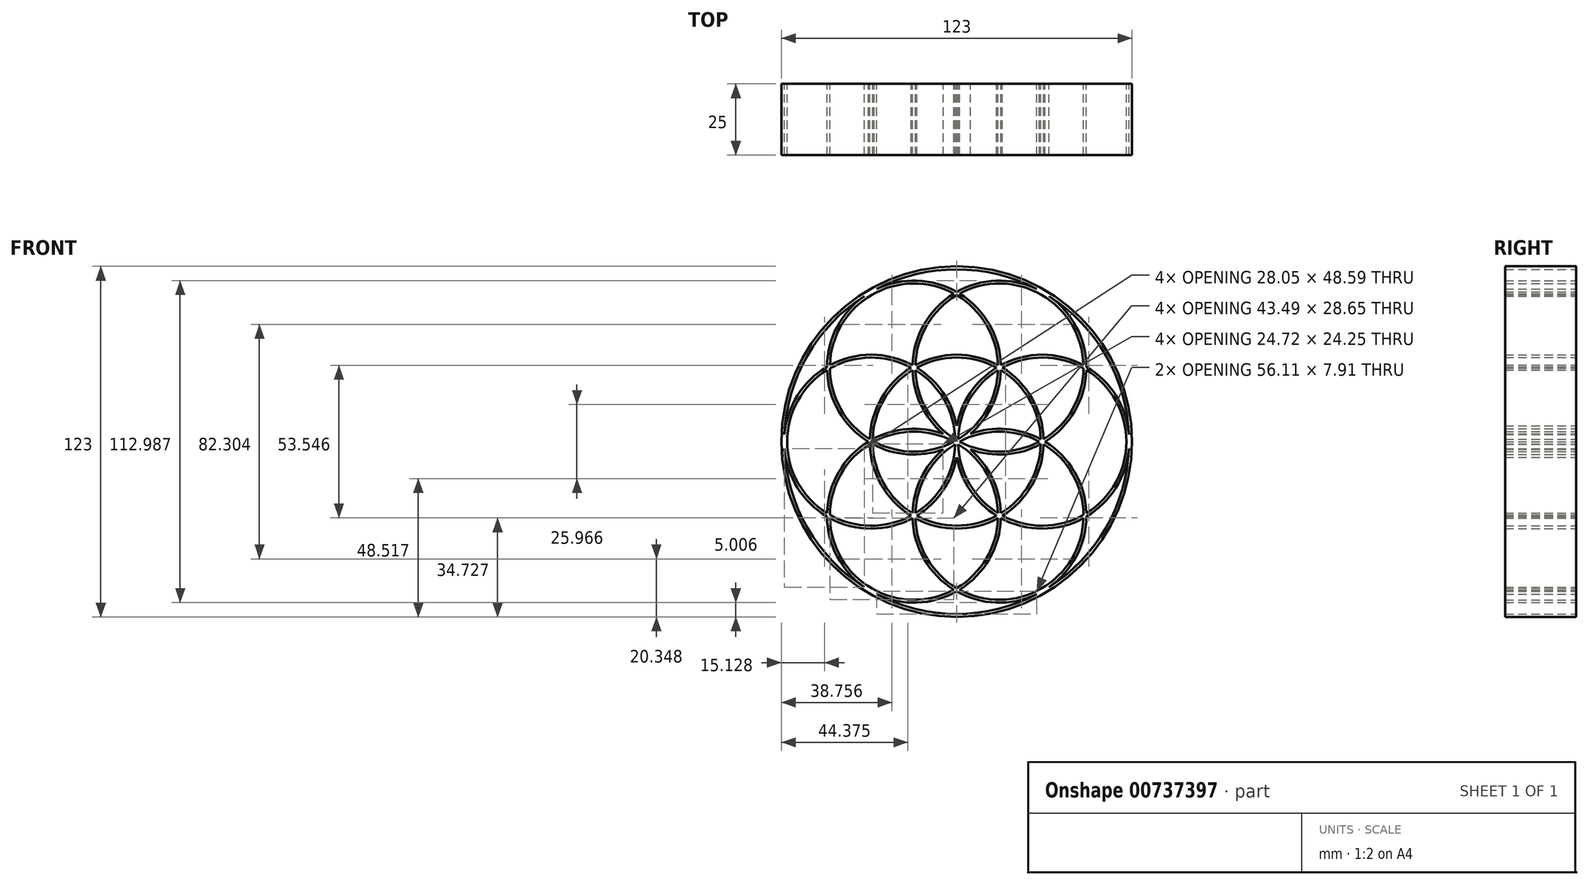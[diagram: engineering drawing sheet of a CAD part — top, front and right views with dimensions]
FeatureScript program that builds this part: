
annotation { "Feature Type Name" : "Feature", "Feature Type Description" : "" }
export const myFeature = defineFeature(function(context is Context, id is Id, definition is map)
    precondition{}
    {
        {
            var Q0;
            Q0=qCreatedBy(makeId("Front.planeOp"),FACE);
            var sketch = newSketch(context, id + "F0", { "sketchPlane" : qUnion([Q0])});
            skArc(sketch, "E0", {"start": v(14.49, 26.84) * mm, "mid": v(0, 30.5) * mm, "end": v(-14.49, 26.84) * mm});
            skArc(sketch, "E1", {"start": v(14, 25.97) * mm, "mid": v(0, 29.5) * mm, "end": v(-14, 25.97) * mm});
            skCircle(sketch, "E2", {"center": v(0, 0) * mm, "radius": 30 * mm, "construction": true});
            skLineSegment(sketch, "E3", {"start": v(0, 0) * mm, "end": v(0, 50.88) * mm, "construction": true});
            skLineSegment(sketch, "E4", {"start": v(0, 0) * mm, "end": v(-40.85, 0) * mm, "construction": true});
            skLineSegment(sketch, "E5", {"start": v(0, 0) * mm, "end": v(-19.65, 34.03) * mm, "construction": true});
            skCircle(sketch, "E6", {"center": v(-15, 25.98) * mm, "radius": 30 * mm, "construction": true});
            skArc(sketch, "E7.1.0", {"start": v(0, 5.5) * mm, "mid": v(-4.83, 17.22) * mm, "end": v(-14, 25.97) * mm});
            skCircle(sketch, "E7.1.1", {"center": v(-30, 0) * mm, "radius": 30 * mm, "construction": true});
            skCircle(sketch, "E7.2.1", {"center": v(-15, -25.98) * mm, "radius": 30 * mm, "construction": true});
            skArc(sketch, "E7.3.0", {"start": v(-4.76, -2.75) * mm, "mid": v(-12.5, -12.79) * mm, "end": v(-15.49, -25.1) * mm});
            skCircle(sketch, "E7.3.1", {"center": v(15, -25.98) * mm, "radius": 30 * mm, "construction": true});
            skCircle(sketch, "E7.4.1", {"center": v(30, 0) * mm, "radius": 30 * mm, "construction": true});
            skArc(sketch, "E7.4.2", {"start": v(0.51, -0.89) * mm, "mid": v(4.45, -14.75) * mm, "end": v(14.49, -25.1) * mm});
            skArc(sketch, "E7.5.0", {"start": v(4.76, -2.75) * mm, "mid": v(17.33, -4.43) * mm, "end": v(29.49, -0.86) * mm});
            skCircle(sketch, "E7.5.1", {"center": v(15, 25.98) * mm, "radius": 30 * mm, "construction": true});
            skArc(sketch, "E7.5.2", {"start": v(1.03, 0) * mm, "mid": v(15, -3.52) * mm, "end": v(28.97, 0) * mm});
            skArc(sketch, "E8.trimOffspring", {"start": v(0, -5.5) * mm, "mid": v(4.83, -17.22) * mm, "end": v(14, -25.97) * mm});
            skArc(sketch, "E9.trimOffspring", {"start": v(-4.76, 2.75) * mm, "mid": v(-17.33, 4.43) * mm, "end": v(-29.49, 0.86) * mm});
            skArc(sketch, "E10.trimOffspring", {"start": v(4.76, 2.75) * mm, "mid": v(12.5, 12.79) * mm, "end": v(15.49, 25.1) * mm});
            skArc(sketch, "E11.trimOffspring", {"start": v(0.51, 0.89) * mm, "mid": v(10.55, 11.23) * mm, "end": v(14.49, 25.1) * mm});
            skArc(sketch, "E12.trimOffspring", {"start": v(-0.5, -0.9) * mm, "mid": v(-10.53, -11.24) * mm, "end": v(-14.47, -25.1) * mm});
            skArc(sketch, "E13.trimOffspring", {"start": v(-1.03, 0) * mm, "mid": v(-15, 3.52) * mm, "end": v(-28.97, 0) * mm});
            skArc(sketch, "E14.trimOffspring", {"start": v(-0.5, 0.88) * mm, "mid": v(-4.44, 14.75) * mm, "end": v(-14.49, 25.1) * mm});
            skArc(sketch, "E15.trimOffspring", {"start": v(14.49, 26.84) * mm, "mid": v(10.4, 40.98) * mm, "end": v(0, 51.38) * mm});
            skArc(sketch, "E16.trimOffspring", {"start": v(15.49, 26.83) * mm, "mid": v(11.42, 41.22) * mm, "end": v(1, 51.95) * mm});
            skArc(sketch, "E17.trimOffspring", {"start": v(14, 25.97) * mm, "mid": v(4.83, 17.22) * mm, "end": v(0, 5.5) * mm});
            skArc(sketch, "E18.trimOffspring", {"start": v(14.49, 25.1) * mm, "mid": v(4.45, 14.75) * mm, "end": v(0.51, 0.89) * mm});
            skArc(sketch, "E19.trimOffspring", {"start": v(30.98, 0) * mm, "mid": v(41.4, 10.72) * mm, "end": v(45.49, 25.1) * mm});
            skArc(sketch, "E20.trimOffspring", {"start": v(28.97, 0) * mm, "mid": v(15, 3.52) * mm, "end": v(1.03, 0) * mm});
            skArc(sketch, "E21.trimOffspring", {"start": v(30.49, 0.87) * mm, "mid": v(40.69, 11.48) * mm, "end": v(44.5, 25.7) * mm});
            skArc(sketch, "E22.trimOffspring", {"start": v(29.49, 0.86) * mm, "mid": v(17.33, 4.43) * mm, "end": v(4.76, 2.75) * mm});
            skArc(sketch, "E23.trimOffspring", {"start": v(30.49, 0.87) * mm, "mid": v(26.41, 15.25) * mm, "end": v(16, 25.97) * mm});
            skArc(sketch, "E24.trimOffspring", {"start": v(29.49, 0.86) * mm, "mid": v(25.55, 14.75) * mm, "end": v(15.49, 25.1) * mm});
            skArc(sketch, "E25.trimOffspring", {"start": v(14.49, -25.1) * mm, "mid": v(10.55, -11.23) * mm, "end": v(0.51, -0.89) * mm});
            skArc(sketch, "E26.trimOffspring", {"start": v(15.49, -25.1) * mm, "mid": v(25.55, -14.75) * mm, "end": v(29.49, -0.86) * mm});
            skArc(sketch, "E27.trimOffspring", {"start": v(15.49, -25.1) * mm, "mid": v(12.5, -12.79) * mm, "end": v(4.76, -2.75) * mm});
            skArc(sketch, "E28.trimOffspring", {"start": v(16, -25.97) * mm, "mid": v(30.28, -29.5) * mm, "end": v(44.5, -25.7) * mm});
            skArc(sketch, "E29.trimOffspring", {"start": v(16, -25.97) * mm, "mid": v(26.41, -15.25) * mm, "end": v(30.49, -0.87) * mm});
            skArc(sketch, "E30.trimOffspring", {"start": v(15.49, -26.83) * mm, "mid": v(29.99, -30.5) * mm, "end": v(44.49, -26.84) * mm});
            skArc(sketch, "E31.trimOffspring", {"start": v(-14.47, -25.1) * mm, "mid": v(-4.44, -14.76) * mm, "end": v(-0.5, -0.9) * mm});
            skArc(sketch, "E32.trimOffspring", {"start": v(-14, -25.97) * mm, "mid": v(0, -29.5) * mm, "end": v(14, -25.97) * mm});
            skArc(sketch, "E33.trimOffspring", {"start": v(-15.49, -26.83) * mm, "mid": v(-11.42, -41.22) * mm, "end": v(-1, -51.95) * mm});
            skArc(sketch, "E34.trimOffspring", {"start": v(-14.49, -26.84) * mm, "mid": v(0, -30.5) * mm, "end": v(14.49, -26.84) * mm});
            skArc(sketch, "E35.trimOffspring", {"start": v(-14.49, -26.84) * mm, "mid": v(-10.4, -40.98) * mm, "end": v(0, -51.38) * mm});
            skArc(sketch, "E36.trimOffspring", {"start": v(-14, -25.97) * mm, "mid": v(-4.83, -17.22) * mm, "end": v(0, -5.5) * mm});
            skArc(sketch, "E37.trimOffspring", {"start": v(-30.98, 0) * mm, "mid": v(-41.4, -10.72) * mm, "end": v(-45.49, -25.1) * mm});
            skArc(sketch, "E38.trimOffspring", {"start": v(-30.49, -0.87) * mm, "mid": v(-40.69, -11.48) * mm, "end": v(-44.5, -25.7) * mm});
            skArc(sketch, "E39.trimOffspring", {"start": v(-30.49, -0.87) * mm, "mid": v(-26.4, -15.26) * mm, "end": v(-15.99, -25.97) * mm});
            skArc(sketch, "E40.trimOffspring", {"start": v(-29.49, -0.86) * mm, "mid": v(-25.55, -14.75) * mm, "end": v(-15.49, -25.1) * mm});
            skArc(sketch, "E41.trimOffspring", {"start": v(-29.49, -0.86) * mm, "mid": v(-17.33, -4.43) * mm, "end": v(-4.76, -2.75) * mm});
            skArc(sketch, "E42.trimOffspring", {"start": v(-28.97, 0) * mm, "mid": v(-15, -3.52) * mm, "end": v(-1.03, 0) * mm});
            skArc(sketch, "E43.trimOffspring", {"start": v(-15.49, 26.83) * mm, "mid": v(-29.99, 30.5) * mm, "end": v(-44.49, 26.84) * mm});
            skArc(sketch, "E44.trimOffspring", {"start": v(-16, 25.97) * mm, "mid": v(-26.41, 15.25) * mm, "end": v(-30.49, 0.87) * mm});
            skArc(sketch, "E45.trimOffspring", {"start": v(-16, 25.97) * mm, "mid": v(-30.29, 29.5) * mm, "end": v(-44.5, 25.68) * mm});
            skArc(sketch, "E46.trimOffspring", {"start": v(-15.49, 25.1) * mm, "mid": v(-12.5, 12.79) * mm, "end": v(-4.76, 2.75) * mm});
            skArc(sketch, "E47.trimOffspring", {"start": v(-15.49, 25.1) * mm, "mid": v(-25.55, 14.75) * mm, "end": v(-29.49, 0.86) * mm});
            skArc(sketch, "E48.trimOffspring", {"start": v(-14.49, 25.1) * mm, "mid": v(-10.54, 11.22) * mm, "end": v(-0.5, 0.88) * mm});
            skArc(sketch, "E49.trimOffspring", {"start": v(-1, 51.95) * mm, "mid": v(-11.42, 41.22) * mm, "end": v(-15.49, 26.83) * mm});
            skArc(sketch, "E50.trimOffspring", {"start": v(0, 52.54) * mm, "mid": v(-13.9, 56.46) * mm, "end": v(-28.05, 53.55) * mm});
            skArc(sketch, "E51.trimOffspring", {"start": v(0, 51.38) * mm, "mid": v(-10.4, 40.98) * mm, "end": v(-14.49, 26.84) * mm});
            skArc(sketch, "E52.trimOffspring", {"start": v(-1, 51.95) * mm, "mid": v(-29.75, 51.53) * mm, "end": v(-44.49, 26.84) * mm});
            skArc(sketch, "E53.trimOffspring", {"start": v(44.49, 26.84) * mm, "mid": v(29.99, 30.5) * mm, "end": v(15.49, 26.83) * mm});
            skArc(sketch, "E54.trimOffspring", {"start": v(44.49, 26.84) * mm, "mid": v(29.75, 51.53) * mm, "end": v(1, 51.95) * mm});
            skArc(sketch, "E55.trimOffspring", {"start": v(44.5, 25.7) * mm, "mid": v(30.28, 29.5) * mm, "end": v(16, 25.97) * mm});
            skArc(sketch, "E56.trimOffspring", {"start": v(45.5, 26.27) * mm, "mid": v(41.94, 40.27) * mm, "end": v(32.35, 51.07) * mm});
            skArc(sketch, "E57.trimOffspring", {"start": v(45.49, -25.1) * mm, "mid": v(59.5, 0) * mm, "end": v(45.49, 25.1) * mm});
            skArc(sketch, "E58.trimOffspring", {"start": v(45.49, -25.1) * mm, "mid": v(41.4, -10.72) * mm, "end": v(30.98, 0) * mm});
            skArc(sketch, "E59.trimOffspring", {"start": v(45.5, -26.27) * mm, "mid": v(55.85, -16.19) * mm, "end": v(60.4, -2.48) * mm});
            skArc(sketch, "E60.trimOffspring", {"start": v(44.5, -25.7) * mm, "mid": v(40.69, -11.48) * mm, "end": v(30.49, -0.87) * mm});
            skArc(sketch, "E61.trimOffspring", {"start": v(0, -51.38) * mm, "mid": v(10.4, -40.98) * mm, "end": v(14.49, -26.84) * mm});
            skArc(sketch, "E62.trimOffspring", {"start": v(1, -51.95) * mm, "mid": v(29.75, -51.53) * mm, "end": v(44.49, -26.84) * mm});
            skArc(sketch, "E63.trimOffspring", {"start": v(1, -51.95) * mm, "mid": v(11.42, -41.22) * mm, "end": v(15.49, -26.83) * mm});
            skArc(sketch, "E64.trimOffspring", {"start": v(0, -52.54) * mm, "mid": v(13.9, -56.46) * mm, "end": v(28.05, -53.55) * mm});
            skArc(sketch, "E65.trimOffspring", {"start": v(-44.5, -25.7) * mm, "mid": v(-30.28, -29.5) * mm, "end": v(-15.99, -25.97) * mm});
            skArc(sketch, "E66.trimOffspring", {"start": v(-45.5, -26.27) * mm, "mid": v(-41.94, -40.27) * mm, "end": v(-32.35, -51.07) * mm});
            skArc(sketch, "E67.trimOffspring", {"start": v(-44.49, -26.84) * mm, "mid": v(-29.99, -30.5) * mm, "end": v(-15.49, -26.83) * mm});
            skArc(sketch, "E68.trimOffspring", {"start": v(-44.49, -26.84) * mm, "mid": v(-29.75, -51.53) * mm, "end": v(-1, -51.95) * mm});
            skArc(sketch, "E69.trimOffspring", {"start": v(-45.5, 26.27) * mm, "mid": v(-55.85, 16.19) * mm, "end": v(-60.4, 2.48) * mm});
            skArc(sketch, "E70.trimOffspring", {"start": v(-44.5, 25.68) * mm, "mid": v(-40.69, 11.47) * mm, "end": v(-30.49, 0.87) * mm});
            skArc(sketch, "E71.trimOffspring", {"start": v(-45.49, 25.1) * mm, "mid": v(-41.4, 10.71) * mm, "end": v(-30.98, 0) * mm});
            skArc(sketch, "E72.trimOffspring", {"start": v(-45.49, 25.1) * mm, "mid": v(-59.49, 0) * mm, "end": v(-45.49, -25.1) * mm});
            skArc(sketch, "E73.0", {"start": v(-32.35, 51.07) * mm, "mid": v(-52.35, 30.23) * mm, "end": v(-60.4, 2.48) * mm});
            skArc(sketch, "E74.trimOffspring", {"start": v(-32.35, 51.07) * mm, "mid": v(-41.94, 40.27) * mm, "end": v(-45.5, 26.27) * mm});
            skArc(sketch, "E75.trimOffspring", {"start": v(28.05, 53.55) * mm, "mid": v(13.9, 56.46) * mm, "end": v(0, 52.54) * mm});
            skArc(sketch, "E76.trimOffspring", {"start": v(28.05, 53.55) * mm, "mid": v(0, 60.45) * mm, "end": v(-28.05, 53.55) * mm});
            skArc(sketch, "E77.trimOffspring", {"start": v(60.4, 2.48) * mm, "mid": v(55.85, 16.19) * mm, "end": v(45.5, 26.27) * mm});
            skArc(sketch, "E78.trimOffspring", {"start": v(60.4, 2.48) * mm, "mid": v(52.35, 30.23) * mm, "end": v(32.35, 51.07) * mm});
            skArc(sketch, "E79.trimOffspring", {"start": v(32.35, -51.07) * mm, "mid": v(41.94, -40.27) * mm, "end": v(45.5, -26.27) * mm});
            skArc(sketch, "E80.trimOffspring", {"start": v(32.35, -51.07) * mm, "mid": v(52.35, -30.22) * mm, "end": v(60.4, -2.48) * mm});
            skArc(sketch, "E81.trimOffspring", {"start": v(-28.05, -53.55) * mm, "mid": v(-13.9, -56.46) * mm, "end": v(0, -52.54) * mm});
            skArc(sketch, "E82.trimOffspring", {"start": v(-28.05, -53.55) * mm, "mid": v(0, -60.45) * mm, "end": v(28.05, -53.55) * mm});
            skArc(sketch, "E83.trimOffspring", {"start": v(-60.4, -2.48) * mm, "mid": v(-55.85, -16.19) * mm, "end": v(-45.5, -26.27) * mm});
            skArc(sketch, "E84.trimOffspring", {"start": v(-60.4, -2.48) * mm, "mid": v(-52.35, -30.23) * mm, "end": v(-32.35, -51.07) * mm});
            skCircle(sketch, "E85", {"center": v(0, 0) * mm, "radius": 61.5 * mm});
            skSolve(sketch);
        }
        {
            var Q0;
            Q0 = qSketchRegion(id + "F0", true);
            extrude(context, id + "F1", {"entities" : qUnion([Q0]), "depth" : 25 * mm, "offsetDistance" : 25 * mm});
        }
    });
